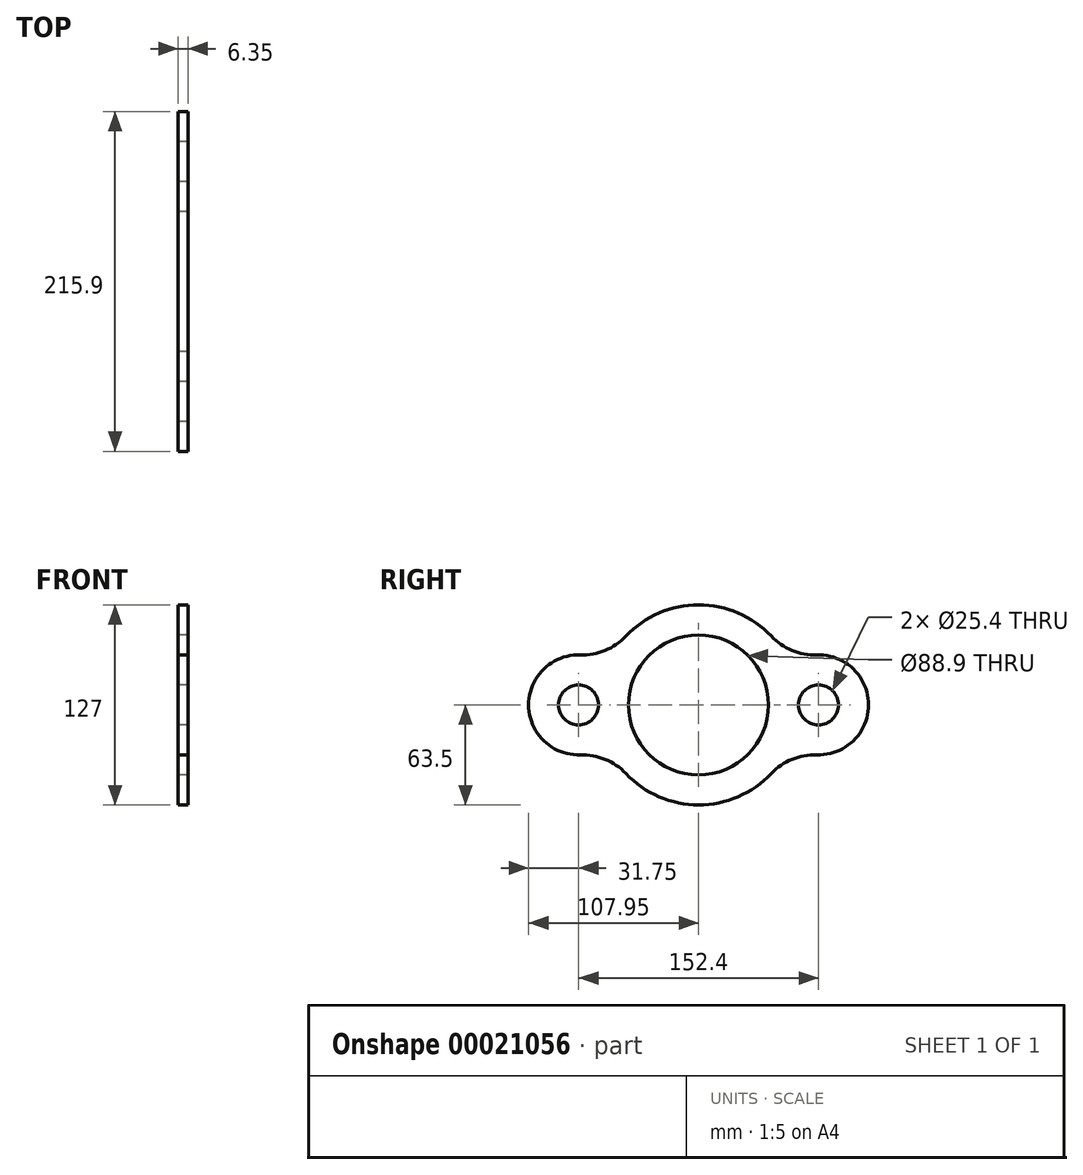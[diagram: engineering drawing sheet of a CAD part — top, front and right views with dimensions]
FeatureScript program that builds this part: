
annotation { "Feature Type Name" : "Feature", "Feature Type Description" : "" }
export const myFeature = defineFeature(function(context is Context, id is Id, definition is map)
    precondition{}
    {
        {
            var Q0;
            Q0=qCreatedBy(makeId("Right.planeOp"),FACE);
            var sketch = newSketch(context, id + "F0", { "sketchPlane" : qUnion([Q0])});
            skCircle(sketch, "E0", {"center": v(0, 0) * mm, "radius": 44.45 * mm});
            skArc(sketch, "E1", {"start": v(-46.14, -43.63) * mm, "mid": v(0, -63.5) * mm, "end": v(46.14, -43.63) * mm});
            skCircle(sketch, "E2", {"center": v(-76.2, 0) * mm, "radius": 12.7 * mm});
            skArc(sketch, "E3", {"start": v(-75.12, 31.73) * mm, "mid": v(-107.95, 0) * mm, "end": v(-75.12, -31.73) * mm});
            skCircle(sketch, "E4", {"center": v(76.2, 0) * mm, "radius": 12.7 * mm});
            skArc(sketch, "E5", {"start": v(75.12, -31.73) * mm, "mid": v(107.95, 0) * mm, "end": v(75.12, 31.73) * mm});
            skArc(sketch, "E6.trimOffspring", {"start": v(46.14, 43.63) * mm, "mid": v(0, 63.5) * mm, "end": v(-46.14, 43.63) * mm});
            skPoint(sketch, "E7.visualSharp", {"position": v(-57.94, 25.98) * mm});
            skArc(sketch, "E7.filletArc", {"start": v(-75.12, 31.73) * mm, "mid": v(-59.35, 34.56) * mm, "end": v(-46.14, 43.63) * mm});
            skPoint(sketch, "E8.visualSharp", {"position": v(57.94, 25.98) * mm});
            skArc(sketch, "E8.filletArc", {"start": v(46.14, 43.63) * mm, "mid": v(59.35, 34.56) * mm, "end": v(75.12, 31.73) * mm});
            skPoint(sketch, "E9.visualSharp", {"position": v(57.94, -25.98) * mm});
            skArc(sketch, "E9.filletArc", {"start": v(75.12, -31.73) * mm, "mid": v(59.35, -34.56) * mm, "end": v(46.14, -43.63) * mm});
            skPoint(sketch, "E10.visualSharp", {"position": v(-57.94, -25.98) * mm});
            skArc(sketch, "E10.filletArc", {"start": v(-46.14, -43.63) * mm, "mid": v(-59.35, -34.56) * mm, "end": v(-75.12, -31.73) * mm});
            skSolve(sketch);
        }
        {
            var Q0;
            Q0=makeQuery(id+"F0.imprint","IMPRINT",FACE,{"disambiguationData":[TD([[makeQuery(id+"F0.imprint","IMPRINT",EDGE,{"derivedFrom":sQuery(id+"F0.wireOp",EDGE,"E1")}),1.0]])]});
            extrude(context, id + "F1", {"entities" : qUnion([Q0]), "depth" : 6.35 * mm});
        }
    });
